# Revit family: Hager-GAMMA-Surface_mounted-IP30-Without_Cover-With_DIN-Hosted-SE-en
name_source: partatom
category: Electrical Equipment
units: mm (PartAtom-declared; Revit-internal decimal feet)

## family parameters
Cut with Voids When Loaded = No
Host = Face
Maintain Annotation Orientation = Yes
Panel Configuration = Two Columns, Circuits Across
Part Type = Panelboard
Room Calculation Point = No
Round Connector Dimension = Use Diameter
Shared = No

## types (8) — shared parameters
BC_MODEL_ID = 1554309
BC_OBJECT_ID = 513865
BC_OBJECT_VERSION = #1
Code hager = ADD-EC000214_EU
EF000003 - Mounting method = Surface mounted
EF000024 - UV resistant = No
EF000049 - Depth = 103 mm  [stored 0.337927 ft]
EF000116 - RAL-number = 9010
EF000118 - With mounting plate = No
EF001062 - EMC-version = No
EF001134 - DIN-rail = Yes
EF005474 - Degree of protection (IP) = IP30
EF006244 - Transparent cover/door = No
EF006306 - With lock = No
EF015777 - Neutral terminal block = Yes
EF015941 - Signal passing door = Yes
ETIM class code = EC000214
ETIM class name = Small distribution board
HG000001-Number of columns = 1
HG000002-With door or cover = No
HG000003-Range = GAMMA
HG000005-Thickness = 2 mm  [stored 0.00656168 ft]
HG000006-Flush mounted = No
HG000009-Double swing door = No
HG000010-Asymmetric doors = No
HG000011-Empty rows from bottom = No
HG000012-Door swing angle = 90.00°
HG000013-Door on the left = No
HG000014-Door on the right = Yes
HG000015-Clearance visibility = Yes
HG000016-Door 3D visibility = Yes
HG000017-Distance between poles = 18 mm  [stored 0.0590551 ft]
HG000060-RAL-number = 9010
HG000099-Onfly Template ID = 507532
Manufacturer = Hager
Name = GAMMA-Surface_mounted-IP30-Without_Cover-With_DIN-SE
Name BIM&CO = Electricity
Name hager = ADD_Enclosures_EC000214
Uniformat = Low Tension Service & Dist.
Uniformat code = D501001
zero-valued in all types: Default Elevation, EF000218 - Built-in depth, EF000332 - Built-in height, EF000846 - Built-in width, EF001131 - Inner depth, HG000007-Number of empty columns, HG000008-Number of empty rows

## per-type parameters (varying)
| type | BC_VARIANT_ID | EF000007 - Colour | EF000008 - Width | EF000040 - Height | EF000266 - Number of rows | EF001088 - Extension possible | EF002950 - Width in number of modular spacings | EF004462 - Type of closure | EF009212 - Cover model | EF015776 - Earthing terminal block | HG000004-Manufacturer reference | HGEF000266-Number of rows | HGEF002950-Width in number of modular spacings |
| GAMMA-Surface_mounted_W250_H250_D103_13_Modular_Spacing-GD113S | 1178868 |  | 250 mm  [stored 0.82021 ft] | 250 mm  [stored 0.82021 ft] | 1 | No | 13 |  |  | No | GD113S | 1 | 13 |
| GAMMA-Surface_mounted_W355_H250_D103_18_Modular_Spacing-GD118S | 1178869 | White | 355 mm  [stored 1.1647 ft] | 250 mm  [stored 0.82021 ft] | 1 | Yes | 18 | Other | With notch | Yes | GD118S | 1 | 18 |
| GAMMA-Surface_mounted_W250_H375_D103_13_Modular_Spacing-GD213S | 1178870 | White | 250 mm  [stored 0.82021 ft] | 375 mm  [stored 1.23031 ft] | 2 | Yes | 13 | Other | With notch | Yes | GD213S | 2 | 13 |
| GAMMA-Surface_mounted_W355_H375_D103_18_Modular_Spacing-GD218S | 1178871 | White | 355 mm  [stored 1.1647 ft] | 375 mm  [stored 1.23031 ft] | 2 | Yes | 18 | Other | With notch | Yes | GD218S | 2 | 18 |
| GAMMA-Surface_mounted_W250_H500_D103_13_Modular_Spacing-GD313S | 1178872 | White | 250 mm  [stored 0.82021 ft] | 500 mm  [stored 1.64042 ft] | 3 | Yes | 13 | Other | With notch | Yes | GD313S | 3 | 13 |
| GAMMA-Surface_mounted_W355_H500_D103_18_Modular_Spacing-GD318S | 1178873 |  | 355 mm  [stored 1.1647 ft] | 500 mm  [stored 1.64042 ft] | 3 | No | 18 |  |  | No | GD318S | 3 | 18 |
| GAMMA-Surface_mounted_W250_H625_D103_13_Modular_Spacing-GD413S | 1178874 |  | 250 mm  [stored 0.82021 ft] | 625 mm  [stored 2.05052 ft] | 4 | No | 13 |  |  | No | GD413S | 4 | 13 |
| GAMMA-Surface_mounted_W355_H625_D103_18_Modular_Spacing-GD418S | 1178875 | White | 355 mm  [stored 1.1647 ft] | 625 mm  [stored 2.05052 ft] | 4 | Yes | 18 | Other | With notch | Yes | GD418S | 4 | 18 |

note: column(s) folded — value = type name in every type: Reference

note: [stored X ft] marks values corroborated as IEEE doubles in the binary element streams (Revit-internal decimal feet)

## geometry (parser evidence)
native form markers: Sweep x13
no freeform markers — native parametric forms only
